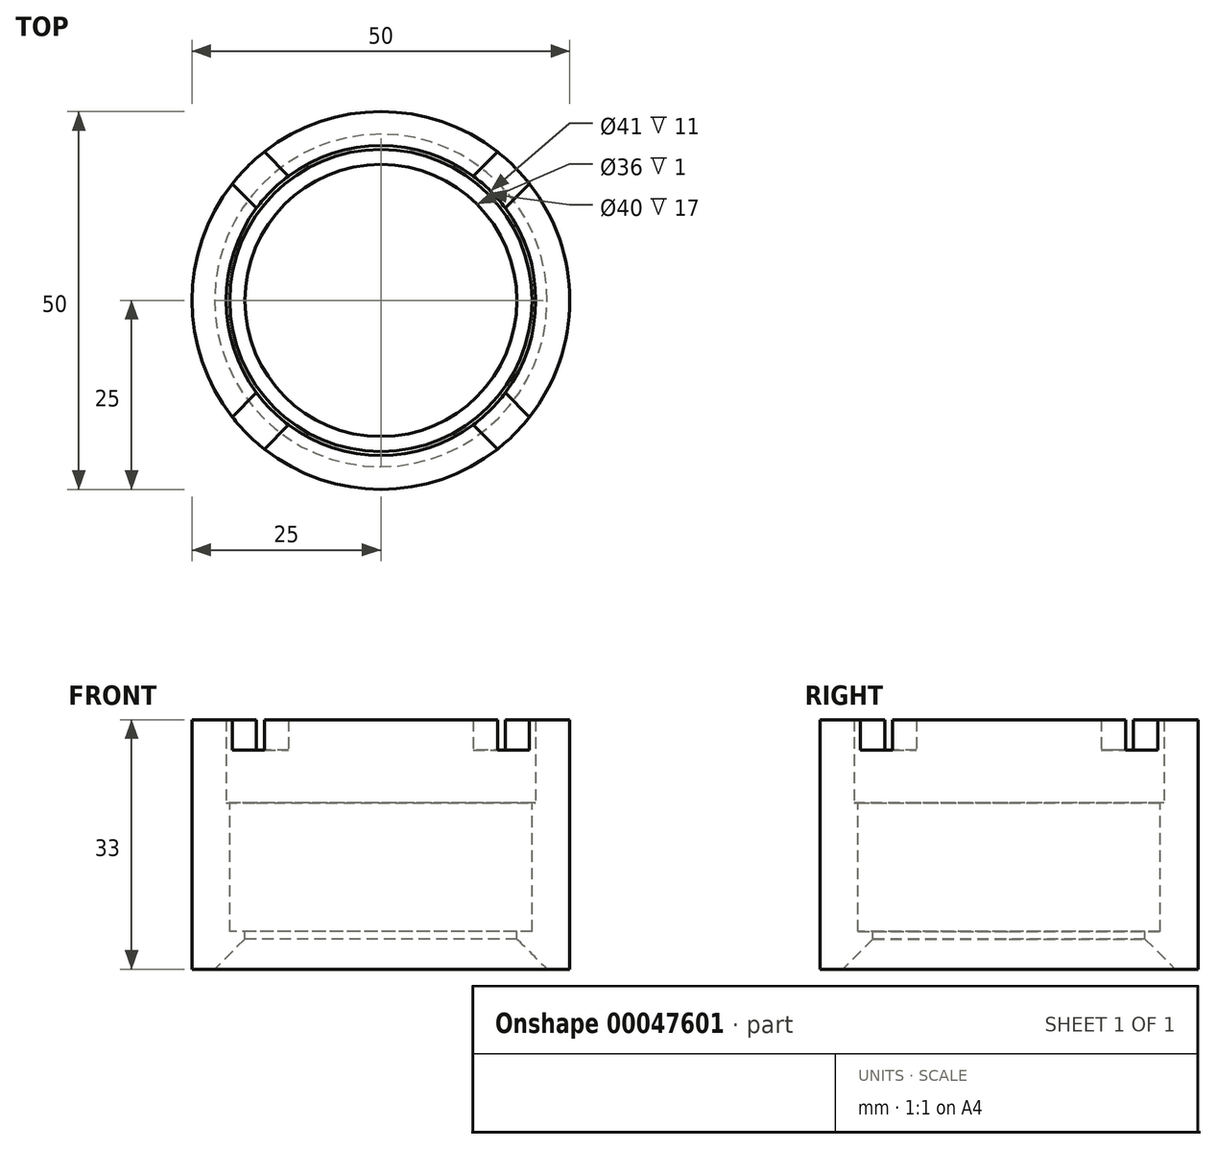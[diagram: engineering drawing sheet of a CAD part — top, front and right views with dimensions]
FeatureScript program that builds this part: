
annotation { "Feature Type Name" : "Feature", "Feature Type Description" : "" }
export const myFeature = defineFeature(function(context is Context, id is Id, definition is map)
    precondition{}
    {
        {
            var Q0;
            Q0=qCreatedBy(makeId("Top.planeOp"),FACE);
            var sketch = newSketch(context, id + "F0", { "sketchPlane" : qUnion([Q0])});
            skCircle(sketch, "E0", {"center": v(0, 0) * mm, "radius": 27 * mm});
            skCircle(sketch, "E1", {"center": v(0, 0) * mm, "radius": 18 * mm});
            skSolve(sketch);
        }
        {
            var Q0;
            Q0=makeQuery(id+"F0.imprint","IMPRINT",FACE,{"disambiguationData":[TD([[makeQuery(id+"F0.imprint","IMPRINT",EDGE,{"derivedFrom":sQuery(id+"F0.wireOp",EDGE,"E0")}),1.0]])]});
            extrude(context, id + "F1", {"entities" : qUnion([Q0]), "oppositeDirection" : true, "depth" : 22 * mm});
        }
        {
            var Q0;
            Q0=makeQuery(id+"F1.opExtrude","CAP_FACE",FACE,{"disambiguationData":[OSD([sQuery(id+"F0.wireOp",EDGE,"E0"),sQuery(id+"F0.wireOp",EDGE,"E1")])],"isStart":true});
            var sketch = newSketch(context, id + "F2", { "sketchPlane" : qUnion([Q0])});
            skCircle(sketch, "E2", {"center": v(0, 0) * mm, "radius": 20 * mm});
            skSolve(sketch);
        }
        {
            var Q0;
            Q0 = qSketchRegion(id + "F2", true);
            extrude(context, id + "F3", {"entities" : qUnion([Q0]), "operationType" : NewBodyOperationType.REMOVE, "oppositeDirection" : true, "depth" : 17 * mm});
        }
        {
            var Q0;
            Q0=makeQuery(id+"F1.opExtrude","CAP_EDGE",EDGE,{"disambiguationData":[OSD([sQuery(id+"F0.wireOp",EDGE,"E1")])],"isStart":false});
            chamfer(context, id + "F4", {"entities" : qUnion([Q0]), "width" : 4 * mm, "tangentPropagation" : true});
        }
        {
            var Q0;
            Q0=qCreatedBy(makeId("Top.planeOp"),FACE);
            var sketch = newSketch(context, id + "F5", { "sketchPlane" : qUnion([Q0])});
            skCircle(sketch, "E3", {"center": v(0, 0) * mm, "radius": 25 * mm});
            skCircle(sketch, "E4.0", {"center": v(0, 0) * mm, "radius": 27 * mm});
            skSolve(sketch);
        }
        {
            var Q0;
            Q0 = qSketchRegion(id + "F5", true);
            extrude(context, id + "F6", {"entities" : qUnion([Q0]), "operationType" : NewBodyOperationType.REMOVE, "oppositeDirection" : true, "depth" : 12 * mm});
        }
        {
            var Q0;
            Q0=makeQuery(id+"F1.opExtrude","CAP_FACE",FACE,{"disambiguationData":[OSD([sQuery(id+"F0.wireOp",EDGE,"E0"),sQuery(id+"F0.wireOp",EDGE,"E1")])],"isStart":true});
            var sketch = newSketch(context, id + "F7", { "sketchPlane" : qUnion([Q0])});
            skCircle(sketch, "E5.0", {"center": v(0, 0) * mm, "radius": 25 * mm});
            skCircle(sketch, "E6", {"center": v(0, 0) * mm, "radius": 20.5 * mm});
            skSolve(sketch);
        }
        {
            var Q0;
            Q0 = qSketchRegion(id + "F7", true);
            extrude(context, id + "F8", {"entities" : qUnion([Q0]), "operationType" : NewBodyOperationType.ADD, "depth" : 11 * mm});
        }
        {
            var Q0;
            Q0=makeQuery(id+"F8.opExtrude","CAP_FACE",FACE,{"disambiguationData":[OSD([sQuery(id+"F7.wireOp",EDGE,"E5.0"),sQuery(id+"F7.wireOp",EDGE,"E6")])],"isStart":false});
            var sketch = newSketch(context, id + "F9", { "sketchPlane" : qUnion([Q0])});
            skLineSegment(sketch, "E7", {"start": v(-32.7, 28.47) * mm, "end": v(30.93, -35.17) * mm});
            skLineSegment(sketch, "E8", {"start": v(30.93, -35.17) * mm, "end": v(35.17, -30.93) * mm});
            skLineSegment(sketch, "E9", {"start": v(35.17, -30.93) * mm, "end": v(-28.47, 32.7) * mm});
            skLineSegment(sketch, "E10", {"start": v(-32.7, 28.47) * mm, "end": v(-28.47, 32.7) * mm});
            skLineSegment(sketch, "E11", {"start": v(-34.57, -30.33) * mm, "end": v(29.07, 33.3) * mm});
            skLineSegment(sketch, "E12", {"start": v(29.07, 33.3) * mm, "end": v(33.3, 29.07) * mm});
            skLineSegment(sketch, "E13", {"start": v(33.3, 29.07) * mm, "end": v(-30.33, -34.57) * mm});
            skLineSegment(sketch, "E14", {"start": v(-34.57, -30.33) * mm, "end": v(-30.33, -34.57) * mm});
            skSolve(sketch);
        }
        {
            var Q0;
            Q0 = qSketchRegion(id + "F9", true);
            extrude(context, id + "F10", {"entities" : qUnion([Q0]), "operationType" : NewBodyOperationType.REMOVE, "oppositeDirection" : true, "depth" : 4 * mm});
        }
        {
            var Q0;
            Q0=makeQuery(id+"F6.boolean.opBoolean","COPY",FACE,{"derivedFrom":makeQuery(id+"F6.opExtrude","CAP_FACE",FACE,{"disambiguationData":[OSD([sQuery(id+"F5.wireOp",EDGE,"E3"),sQuery(id+"F5.wireOp",EDGE,"E4.0")])],"isStart":false})});
            var sketch = newSketch(context, id + "F11", { "sketchPlane" : qUnion([Q0])});
            skCircle(sketch, "E15.0.0", {"center": v(0, 0) * mm, "radius": 27 * mm});
            skCircle(sketch, "E16.0", {"center": v(0, 0) * mm, "radius": 25 * mm});
            skSolve(sketch);
        }
        {
            var Q0;
            Q0 = qSketchRegion(id + "F11", true);
            extrude(context, id + "F12", {"entities" : qUnion([Q0]), "operationType" : NewBodyOperationType.REMOVE, "endBound" : BoundingType.THROUGH_ALL, "oppositeDirection" : true, "depth" : 25 * mm});
        }
    });
